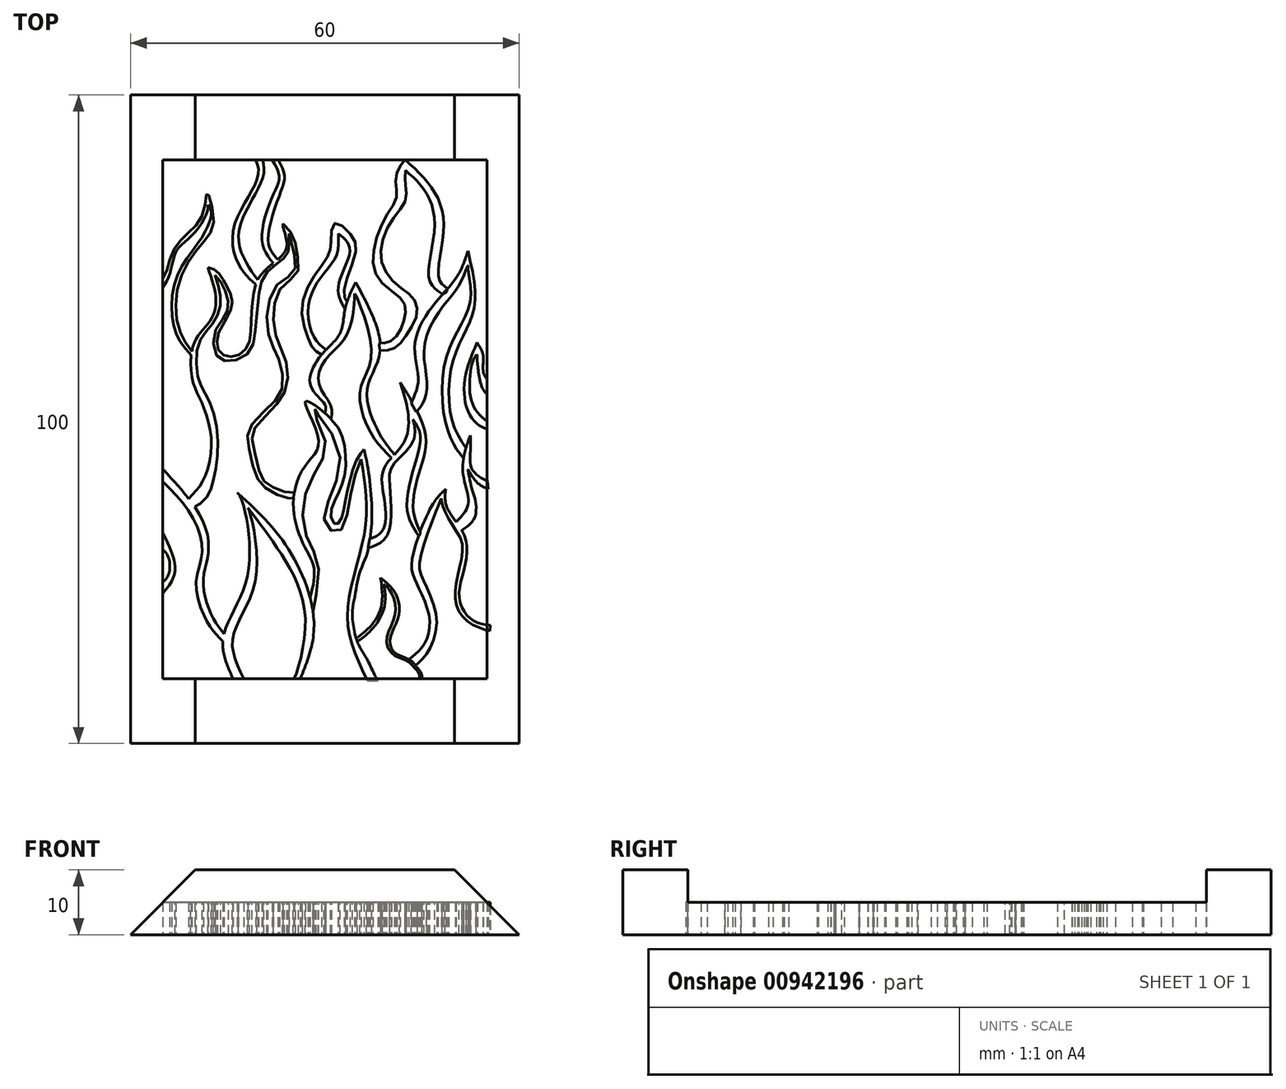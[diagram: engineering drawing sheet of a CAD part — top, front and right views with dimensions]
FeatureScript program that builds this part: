
annotation { "Feature Type Name" : "Feature", "Feature Type Description" : "" }
export const myFeature = defineFeature(function(context is Context, id is Id, definition is map)
    precondition{}
    {
        {
            var Q0;
            Q0=qCreatedBy(makeId("Top.planeOp"),FACE);
            var sketch = newSketch(context, id + "F0", { "sketchPlane" : qUnion([Q0])});
            skLineSegment(sketch, "E0.bottom", {"start": v(35, -50) * mm, "end": v(-35, -50) * mm});
            skLineSegment(sketch, "E0.top", {"start": v(35, 50) * mm, "end": v(-35, 50) * mm});
            skLineSegment(sketch, "E0.left", {"start": v(35, -50) * mm, "end": v(35, 50) * mm});
            skLineSegment(sketch, "E0.right", {"start": v(-35, -50) * mm, "end": v(-35, 50) * mm});
            skPoint(sketch, "E0.middle", {"position": v(0, 0) * mm});
            skLineSegment(sketch, "E1.bottom", {"start": v(25, -40) * mm, "end": v(-25, -40) * mm});
            skLineSegment(sketch, "E1.top", {"start": v(25, 40) * mm, "end": v(-25, 40) * mm});
            skLineSegment(sketch, "E1.left", {"start": v(25, -40) * mm, "end": v(25, 40) * mm});
            skLineSegment(sketch, "E1.right", {"start": v(-25, -40) * mm, "end": v(-25, 40) * mm});
            skSolve(sketch);
        }
        {
            var Q0;
            Q0=makeQuery(id+"F0.imprint","IMPRINT",FACE,{"disambiguationData":[TD([[makeQuery(id+"F0.imprint","IMPRINT",EDGE,{"derivedFrom":sQuery(id+"F0.wireOp",EDGE,"E0.bottom")}),-1.0]])]});
            extrude(context, id + "F1", {"entities" : qUnion([Q0]), "depth" : 10 * mm, "offsetDistance" : 25 * mm});
        }
        {
            var Q0;
            Q0=qCreatedBy(makeId("Top.planeOp"),FACE);
            var sketch = newSketch(context, id + "F2", { "sketchPlane" : qUnion([Q0])});
            skFitSpline(sketch, "E2", {"points": [v(-13.68, -40.96) * mm, v(-15.7, -33.78) * mm, v(-11.88, -23.84) * mm, v(-12.94, -12.18) * mm, v(-13.5, -11.32) * mm], "startDerivative": vector(-13.53, 27.29) * mm, "endDerivative": vector(-5.48, 5.3) * mm});
            skFitSpline(sketch, "E3", {"points": [v(-4.14, -40.79) * mm, v(-1.68, -31.66) * mm, v(-5.82, -19.7) * mm, v(-13.33, -11.5) * mm], "startDerivative": vector(12.17, 28.05) * mm, "endDerivative": vector(-23.9, 21.92) * mm});
            skFitSpline(sketch, "E4", {"points": [v(-12.05, -40.9) * mm, v(-14.21, -33.8) * mm, v(-10.6, -24.24) * mm, v(-11.88, -13.66) * mm, v(-11.96, -13.62) * mm], "startDerivative": vector(-13.14, 24.91) * mm, "endDerivative": vector(-2.3, -0.16) * mm});
            skFitSpline(sketch, "E5", {"points": [v(-11.88, -13.66) * mm, v(-7.03, -20.33) * mm, v(-3, -31.3) * mm, v(-5.12, -40.6) * mm, v(-5.34, -40.6) * mm], "startDerivative": vector(16.42, -21.5) * mm, "endDerivative": vector(-4.05, 2.08) * mm});
            skLineSegment(sketch, "E6", {"start": v(-13.68, -40.96) * mm, "end": v(-12.05, -40.9) * mm});
            skLineSegment(sketch, "E7", {"start": v(-5.27, -40.63) * mm, "end": v(-4.14, -40.79) * mm});
            skFitSpline(sketch, "E8", {"points": [v(6.54, -40.33) * mm, v(3.48, -30.22) * mm, v(6.2, -16.97) * mm, v(5.6, -6.18) * mm], "startDerivative": vector(-14.57, 30.29) * mm, "endDerivative": vector(-5.39, 32.36) * mm});
            skFitSpline(sketch, "E9", {"points": [v(5.6, -6.18) * mm, v(4.25, -10.26) * mm, v(3.06, -16.12) * mm, v(1.7, -17.4) * mm, v(0, -16.04) * mm, v(1.02, -11.45) * mm, v(1.96, -3.97) * mm, v(-1.44, 1.38) * mm, v(-1.36, 1.46) * mm, v(-1.7, 1.38) * mm, v(0, -3.12) * mm, v(-1.02, -7.37) * mm, v(-3.31, -12.98) * mm, v(-2.46, -18.92) * mm, v(-0.93, -23.09) * mm, v(-1.83, -29.73) * mm, v(-1.8, -29.89) * mm], "startDerivative": vector(-21.95, -53.1) * mm, "endDerivative": vector(3.5, -6.25) * mm});
            skFitSpline(sketch, "E10", {"points": [v(-2.28, -27.52) * mm, v(-1.68, -23.08) * mm, v(-3.31, -19.3) * mm, v(-4.88, -12.98) * mm, v(-3, -7.15) * mm, v(-0.95, -3.22) * mm, v(-3, 2.71) * mm, v(0.98, 0) * mm, v(2.98, -3.79) * mm, v(3.13, -8.08) * mm, v(2.05, -11.5) * mm, v(0.91, -14.72) * mm, v(1.7, -16.22) * mm, v(2.55, -15.3) * mm, v(3.27, -11.93) * mm, v(3.89, -9.48) * mm, v(4.85, -6.44) * mm, v(6.03, -4.65) * mm, v(6.07, -4.58) * mm], "startDerivative": vector(19.2, 73.13) * mm, "endDerivative": vector(2, 5.91) * mm});
            skFitSpline(sketch, "E11", {"points": [v(6.03, -4.65) * mm, v(6.64, -7.51) * mm, v(7.21, -12.98) * mm, v(7.14, -17.3) * mm, v(6.39, -21.08) * mm, v(5.21, -24.16) * mm, v(4.67, -27.12) * mm, v(4.25, -29.81) * mm, v(5, -34.3) * mm, v(6.54, -37.12) * mm, v(8.17, -40.33) * mm, v(8.22, -40.33) * mm], "startDerivative": vector(7.1, -29.12) * mm, "endDerivative": vector(3.64, 2.07) * mm});
            skLineSegment(sketch, "E12", {"start": v(6.54, -40.33) * mm, "end": v(8.22, -40.33) * mm});
            skFitSpline(sketch, "E13", {"points": [v(4.83, -33.83) * mm, v(7.26, -31.67) * mm, v(8.82, -28.18) * mm, v(8.58, -24.55) * mm, v(8.55, -24.46) * mm], "startDerivative": vector(8.42, 6.64) * mm, "endDerivative": vector(-0.47, 1) * mm});
            skFitSpline(sketch, "E14", {"points": [v(8.55, -24.46) * mm, v(10.5, -26.26) * mm, v(11.46, -28.66) * mm, v(11.07, -31.3) * mm, v(10.05, -33.98) * mm, v(10.83, -36.02) * mm, v(12.93, -37.01) * mm, v(13.99, -37.97) * mm, v(14.98, -39.53) * mm, v(14.98, -40.02) * mm, v(15.04, -39.97) * mm], "startDerivative": vector(17.16, -13.23) * mm, "endDerivative": vector(3.49, 3.77) * mm});
            skFitSpline(sketch, "E15", {"points": [v(5, -34.3) * mm, v(6.01, -33.57) * mm, v(7.65, -31.96) * mm, v(9.28, -28.26) * mm, v(9.05, -25.37) * mm, v(9, -25.35) * mm], "startDerivative": vector(5.7, 3.92) * mm, "endDerivative": vector(-1.21, 0) * mm});
            skFitSpline(sketch, "E16", {"points": [v(9, -25.35) * mm, v(10.03, -26.43) * mm, v(10.88, -28.62) * mm, v(10.47, -31.3) * mm, v(9.54, -33.87) * mm, v(10.5, -36.27) * mm, v(12.79, -37.29) * mm, v(13.68, -38.18) * mm, v(14.64, -39.52) * mm, v(14.6, -40.15) * mm, v(14.62, -40.15) * mm], "startDerivative": vector(10.85, -9.73) * mm, "endDerivative": vector(2.03, 0.73) * mm});
            skLineSegment(sketch, "E17", {"start": v(14.62, -40.15) * mm, "end": v(15.04, -39.97) * mm});
            skLineSegment(sketch, "E18", {"start": v(-5.12, -40.6) * mm, "end": v(-4.14, -40.79) * mm});
            skFitSpline(sketch, "E19", {"points": [v(-15.56, -33.1) * mm, v(-17.49, -30.22) * mm, v(-18.76, -25.04) * mm, v(-18, -20.58) * mm, v(-19.84, -13.88) * mm, v(-25.8, -6.7) * mm, v(-25.8, -6.55) * mm], "startDerivative": vector(-13.61, 16.83) * mm, "endDerivative": vector(1.72, 3.21) * mm});
            skFitSpline(sketch, "E20", {"points": [v(-15.74, -34.27) * mm, v(-17.05, -32.86) * mm, v(-18.5, -30.61) * mm, v(-19.85, -25.1) * mm, v(-18.92, -20.42) * mm, v(-20.78, -14.5) * mm, v(-25.8, -8.85) * mm], "startDerivative": vector(-12.4, 12.53) * mm, "endDerivative": vector(-25.9, 24.82) * mm});
            skFitSpline(sketch, "E21", {"points": [v(-25.8, -27.84) * mm, v(-23.5, -24.7) * mm, v(-23.4, -21.27) * mm, v(-25.8, -16.02) * mm, v(-25.8, -16.12) * mm], "startDerivative": vector(9, 10.56) * mm, "endDerivative": vector(0.54, -3.22) * mm});
            skFitSpline(sketch, "E22", {"points": [v(-25.8, -25.64) * mm, v(-24.26, -24.26) * mm, v(-24.14, -21.32) * mm, v(-25.8, -19.4) * mm], "startDerivative": vector(5.94, 3.52) * mm, "endDerivative": vector(-6, 4.84) * mm});
            skLineSegment(sketch, "E23", {"start": v(-25.8, -16.02) * mm, "end": v(-25.8, -19.4) * mm});
            skLineSegment(sketch, "E24", {"start": v(-25.8, -25.64) * mm, "end": v(-25.8, -27.84) * mm});
            skLineSegment(sketch, "E25", {"start": v(-25.8, -6.55) * mm, "end": v(-25.8, -8.85) * mm});
            skFitSpline(sketch, "E26", {"points": [v(12.93, -37.01) * mm, v(14.9, -35.28) * mm, v(16.17, -31.12) * mm, v(14.1, -25.17) * mm, v(13.41, -21.86) * mm, v(16.56, -13.28) * mm, v(18.64, -10.78) * mm], "startDerivative": vector(16.34, 11.46) * mm, "endDerivative": vector(14.03, 12.97) * mm});
            skFitSpline(sketch, "E27", {"points": [v(18.64, -10.78) * mm, v(18.7, -13.28) * mm, v(20.28, -15.86) * mm, v(21.85, -19.07) * mm, v(21.42, -23.36) * mm, v(20.7, -27.21) * mm, v(21.64, -29.86) * mm, v(23.35, -31.29) * mm, v(25.2, -31.79) * mm, v(25.5, -31.79) * mm], "startDerivative": vector(-2.35, -23.17) * mm, "endDerivative": vector(5.85, 0.53) * mm});
            skFitSpline(sketch, "E28", {"points": [v(13.99, -37.97) * mm, v(15.62, -36.32) * mm, v(17.24, -31.06) * mm, v(15.22, -24.9) * mm, v(14.66, -21.72) * mm, v(17.5, -13.33) * mm, v(17.97, -12.23) * mm], "startDerivative": vector(13.15, 10.63) * mm, "endDerivative": vector(3.75, 8.26) * mm});
            skFitSpline(sketch, "E29", {"points": [v(17.97, -12.23) * mm, v(18.15, -13.26) * mm, v(19.56, -16.17) * mm, v(21.16, -19.07) * mm, v(20.7, -23.16) * mm, v(20.1, -27.3) * mm, v(21.02, -30.16) * mm, v(23.24, -31.9) * mm, v(25.44, -32.66) * mm, v(25.5, -32.64) * mm], "startDerivative": vector(0.96, -12.29) * mm, "endDerivative": vector(1.87, 1.95) * mm});
            skLineSegment(sketch, "E30", {"start": v(25.44, -32.66) * mm, "end": v(25.5, -31.79) * mm});
            skFitSpline(sketch, "E31", {"points": [v(-21.02, -12.25) * mm, v(-18.72, -9.3) * mm, v(-17.55, -2.84) * mm, v(-19.17, 2.92) * mm, v(-20.38, 5.9) * mm, v(-20.2, 11.72) * mm, v(-17.77, 15.05) * mm, v(-16.8, 18.34) * mm, v(-18.04, 23.41) * mm], "startDerivative": vector(22.52, 22.51) * mm, "endDerivative": vector(-13.58, 40.22) * mm});
            skFitSpline(sketch, "E32", {"points": [v(-18.04, 23.41) * mm, v(-16.54, 22.7) * mm, v(-15.28, 20.77) * mm, v(-14.32, 18.43) * mm, v(-14.98, 15.84) * mm, v(-16.36, 13.32) * mm, v(-16.3, 10.5) * mm, v(-14.32, 9.66) * mm, v(-11.98, 11.1) * mm, v(-11.38, 14.64) * mm, v(-11.14, 18.25) * mm, v(-10.35, 21.5) * mm, v(-7.95, 24.07) * mm, v(-5.9, 26.63) * mm, v(-6.5, 29.82) * mm, v(-6.5, 30.12) * mm], "startDerivative": vector(30.14, -9.52) * mm, "endDerivative": vector(2.2, 9.15) * mm});
            skFitSpline(sketch, "E33", {"points": [v(-6.5, 30.12) * mm, v(-5.1, 28.62) * mm, v(-4.27, 25.5) * mm, v(-4.33, 22.43) * mm, v(-6.61, 20.45) * mm, v(-7.93, 16.66) * mm, v(-7.33, 12.16) * mm, v(-6.01, 8.97) * mm, v(-5.95, 4.89) * mm, v(-8, 1.7) * mm, v(-10.94, -1.6) * mm, v(-11.12, -3.8) * mm, v(-9.91, -8.54) * mm, v(-8.9, -9.98) * mm, v(-6.43, -11.18) * mm, v(-4.72, -11.3) * mm], "startDerivative": vector(28.86, -24.13) * mm, "endDerivative": vector(32.47, 1.3) * mm});
            skFitSpline(sketch, "E34", {"points": [v(-4.84, -12.2) * mm, v(-5.26, -12.17) * mm, v(-6.52, -11.94) * mm, v(-9.35, -10.43) * mm, v(-10.67, -8.54) * mm, v(-11.78, -3.99) * mm, v(-11.63, -1.36) * mm, v(-8.45, 2.06) * mm, v(-6.54, 4.95) * mm, v(-7.03, 9.03) * mm, v(-8.26, 11.7) * mm, v(-8.9, 16.66) * mm, v(-7.03, 21.04) * mm, v(-4.83, 22.7) * mm, v(-4.77, 25.66) * mm, v(-5.5, 28.36) * mm, v(-5.55, 28.62) * mm], "startDerivative": vector(-15.62, 0.83) * mm, "endDerivative": vector(-1.94, 9.71) * mm});
            skFitSpline(sketch, "E35", {"points": [v(-5.54, 28.55) * mm, v(-5.54, 26.6) * mm, v(-5.98, 25.15) * mm, v(-7.72, 23.77) * mm, v(-9.7, 21.45) * mm, v(-10.28, 18.25) * mm, v(-10.67, 14.64) * mm, v(-11.44, 10.7) * mm, v(-14.32, 8.99) * mm, v(-16.54, 9.66) * mm, v(-16.97, 13.43) * mm, v(-15.28, 16.17) * mm, v(-14.92, 18.25) * mm, v(-15.82, 20.77) * mm, v(-16.94, 22.17) * mm], "startDerivative": vector(1.12, -33.36) * mm, "endDerivative": vector(-19.84, 21.36) * mm});
            skFitSpline(sketch, "E36", {"points": [v(-16.94, 22.17) * mm, v(-16.07, 18.25) * mm, v(-17.27, 14.82) * mm, v(-19.43, 11.72) * mm, v(-19.46, 6.1) * mm, v(-18.07, 3.27) * mm, v(-16.54, -2.69) * mm, v(-17.17, -9.3) * mm, v(-18.33, -12.18) * mm, v(-20.09, -13.51) * mm, v(-20.18, -13.38) * mm], "startDerivative": vector(12.64, -36.82) * mm, "endDerivative": vector(-1.95, 8.45) * mm});
            skFitSpline(sketch, "E37", {"points": [v(14.7, -17.3) * mm, v(13.64, -13.94) * mm, v(14.45, -8.54) * mm, v(15.56, -2.69) * mm, v(11.62, 5.7) * mm], "startDerivative": vector(-7.27, 16.15) * mm, "endDerivative": vector(-17.46, 27.77) * mm});
            skFitSpline(sketch, "E38", {"points": [v(11.62, 5.7) * mm, v(12.63, 2.16) * mm, v(12.43, -3.12) * mm, v(9.36, -7.15) * mm, v(8.82, -9.98) * mm, v(9.36, -13.94) * mm, v(8.82, -17.3) * mm, v(7, -18.41) * mm], "startDerivative": vector(7.74, -22.94) * mm, "endDerivative": vector(-19.54, -6.96) * mm});
            skFitSpline(sketch, "E39", {"points": [v(6.74, -19.85) * mm, v(8.07, -19.34) * mm, v(9.57, -17.95) * mm, v(10.24, -14.17) * mm, v(10, -9.9) * mm, v(10.36, -7.32) * mm, v(13.6, -3.48) * mm, v(13.6, 0) * mm], "startDerivative": vector(13.8, 4.22) * mm, "endDerivative": vector(-5.5, 23.35) * mm});
            skFitSpline(sketch, "E40", {"points": [v(13.6, 0) * mm, v(14.74, -2.64) * mm, v(13.6, -7.98) * mm, v(12.7, -13.99) * mm, v(13.6, -16.57) * mm, v(14.45, -17.98) * mm], "startDerivative": vector(8.76, -13.32) * mm, "endDerivative": vector(6.18, -9.74) * mm});
            skFitSpline(sketch, "E41", {"points": [v(20.28, -15.86) * mm, v(22.14, -12.9) * mm, v(21.28, -8.11) * mm, v(22.43, -2.47) * mm], "startDerivative": vector(8.97, 9.37) * mm, "endDerivative": vector(5.32, 15.26) * mm});
            skFitSpline(sketch, "E42", {"points": [v(22.43, -2.47) * mm, v(22.5, -4.33) * mm, v(22.71, -7.69) * mm, v(24.64, -9.33) * mm, v(25.07, -9.47) * mm], "startDerivative": vector(0.68, -6.66) * mm, "endDerivative": vector(2.73, -0.64) * mm});
            skFitSpline(sketch, "E43", {"points": [v(25.21, -10.78) * mm, v(23.57, -9.83) * mm, v(22.07, -7.69) * mm], "startDerivative": vector(-3.75, 1.64) * mm, "endDerivative": vector(-2.57, 4.48) * mm});
            skFitSpline(sketch, "E44", {"points": [v(22.07, -7.9) * mm, v(22.71, -10.78) * mm, v(23.28, -12.97) * mm, v(22.71, -15.86) * mm, v(21.12, -17.14) * mm, v(21.14, -17.18) * mm], "startDerivative": vector(2.3, -11.6) * mm, "endDerivative": vector(1.26, -0.85) * mm});
            skLineSegment(sketch, "E45", {"start": v(25.07, -9.47) * mm, "end": v(25.21, -10.78) * mm});
            skFitSpline(sketch, "E46", {"points": [v(21.77, -4.46) * mm, v(19.56, 0) * mm, v(19.56, 8.19) * mm, v(21.77, 13.75) * mm, v(23.2, 18.3) * mm, v(22.07, 25.97) * mm], "startDerivative": vector(-14.52, 22.01) * mm, "endDerivative": vector(-8.63, 36.95) * mm});
            skFitSpline(sketch, "E47", {"points": [v(22.07, 25.97) * mm, v(20.47, 22.13) * mm, v(16.93, 17.79) * mm, v(13.9, 11.73) * mm, v(14.4, 6.17) * mm, v(13.45, 2.79) * mm], "startDerivative": vector(-6.91, -21.62) * mm, "endDerivative": vector(-8.55, -18.89) * mm});
            skFitSpline(sketch, "E48", {"points": [v(21.38, -6.08) * mm, v(20.01, -4.08) * mm, v(18.51, 0) * mm, v(18.44, 8.35) * mm, v(20.87, 14.28) * mm, v(22.48, 18.35) * mm, v(22.07, 23.07) * mm], "startDerivative": vector(-12, 15.82) * mm, "endDerivative": vector(-5.67, 29.87) * mm});
            skFitSpline(sketch, "E49", {"points": [v(21.8, 23.07) * mm, v(20.37, 20.14) * mm, v(18, 17.14) * mm, v(15.37, 11.43) * mm, v(15.72, 5.92) * mm, v(15.3, 2.79) * mm, v(14.24, 1.25) * mm], "startDerivative": vector(-8.21, -19.86) * mm, "endDerivative": vector(-10.4, -11.91) * mm});
            skFitSpline(sketch, "E50", {"points": [v(21.8, 23.07) * mm, v(22.07, 23.68) * mm, v(22.07, 23.07) * mm], "startDerivative": vector(0.67, 1.83) * mm, "endDerivative": vector(-0.13, -1.86) * mm});
            skFitSpline(sketch, "E51", {"points": [v(-20.54, 10.46) * mm, v(-22.6, 14.22) * mm, v(-22.4, 21.4) * mm, v(-19.07, 26.95) * mm, v(-17.17, 30.5) * mm, v(-18.16, 34.83) * mm, v(-18.66, 32.1) * mm, v(-20.88, 28.87) * mm, v(-23.41, 25.97) * mm, v(-24.72, 22.1) * mm, v(-25.8, 21.1) * mm], "startDerivative": vector(-23.76, 32.34) * mm, "endDerivative": vector(-19.74, -11.85) * mm});
            skFitSpline(sketch, "E52", {"points": [v(-25.43, 19.76) * mm, v(-24.03, 22.1) * mm, v(-22.88, 25.97) * mm, v(-20.3, 28.56) * mm, v(-18.1, 32.1) * mm, v(-18.03, 33.05) * mm], "startDerivative": vector(8.31, 10.66) * mm, "endDerivative": vector(-0.68, 6.9) * mm});
            skFitSpline(sketch, "E53", {"points": [v(-18.03, 33.05) * mm, v(-17.5, 32.1) * mm, v(-17.81, 30.47) * mm, v(-19.46, 27.33) * mm, v(-23, 21.55) * mm, v(-23.14, 13.72) * mm, v(-21.6, 10.97) * mm, v(-20.62, 9.86) * mm], "startDerivative": vector(8.22, -10.57) * mm, "endDerivative": vector(9.73, -10.53) * mm});
            skLineSegment(sketch, "E54", {"start": v(-25.8, 21.1) * mm, "end": v(-25.43, 19.76) * mm});
            skFitSpline(sketch, "E55", {"points": [v(10.28, -5.97) * mm, v(7.21, -2.31) * mm, v(5.45, 4.47) * mm, v(7.21, 10.4) * mm, v(4.67, 19.26) * mm, v(4.6, 19.33) * mm], "startDerivative": vector(-15.6, 15.08) * mm, "endDerivative": vector(-1.73, 0.72) * mm});
            skFitSpline(sketch, "E56", {"points": [v(4.6, 19.33) * mm, v(4.38, 16.69) * mm, v(3.13, 12.55) * mm, v(0, 9.05) * mm, v(-0.9, 5.4) * mm, v(0.88, 2.19) * mm, v(0.98, 0) * mm], "startDerivative": vector(-0.91, -16.9) * mm, "endDerivative": vector(-2.28, -16.26) * mm});
            skFitSpline(sketch, "E57", {"points": [v(10.74, -5.46) * mm, v(9.7, -4.16) * mm, v(8.28, -1.94) * mm, v(6.51, 4.42) * mm, v(8.53, 10.59) * mm, v(4.75, 21.14) * mm], "startDerivative": vector(-9.25, 11.1) * mm, "endDerivative": vector(-20.8, 38.74) * mm});
            skFitSpline(sketch, "E58", {"points": [v(4.75, 21.14) * mm, v(3.13, 17) * mm, v(2.32, 13.21) * mm, v(-0.5, 9.93) * mm, v(-2.22, 5.23) * mm, v(0, 2.25) * mm, v(0, 0.94) * mm], "startDerivative": vector(-10.72, -22.22) * mm, "endDerivative": vector(-3.65, -12.61) * mm});
            skFitSpline(sketch, "E59", {"points": [v(18.19, 19.26) * mm, v(16.1, 21.64) * mm, v(16.93, 29.69) * mm, v(15.37, 35.31) * mm, v(12.43, 38.37) * mm], "startDerivative": vector(-13.95, 9.15) * mm, "endDerivative": vector(-13.94, 12.17) * mm});
            skFitSpline(sketch, "E60", {"points": [v(12.43, 38.37) * mm, v(12.43, 36.16) * mm, v(12.43, 33.78) * mm, v(10.23, 30.47) * mm, v(8.61, 25.37) * mm, v(10.48, 21.3) * mm, v(13.48, 18.83) * mm, v(14.22, 16.37) * mm, v(12.43, 12.71) * mm, v(10.57, 10.84) * mm, v(8.53, 10.59) * mm], "startDerivative": vector(-1.23, -26.61) * mm, "endDerivative": vector(-27.02, 0.36) * mm});
            skFitSpline(sketch, "E61", {"points": [v(18.95, 20.14) * mm, v(17.56, 21.82) * mm, v(18.34, 29.63) * mm, v(16.48, 35.7) * mm, v(12.43, 39.96) * mm], "startDerivative": vector(-11.2, 7.48) * mm, "endDerivative": vector(-16.77, 15.22) * mm});
            skFitSpline(sketch, "E62", {"points": [v(12.34, 40.02) * mm, v(11.26, 38.37) * mm, v(10.96, 36.11) * mm, v(11.02, 34.01) * mm, v(9.27, 31) * mm, v(7.47, 25.36) * mm, v(8.53, 21.3) * mm, v(11.92, 18.45) * mm, v(12.43, 16.6) * mm, v(11.86, 14.13) * mm, v(10.48, 12.27) * mm, v(9.1, 11.73) * mm, v(8.53, 11.79) * mm], "startDerivative": vector(-17.07, -21) * mm, "endDerivative": vector(-12.69, 3.07) * mm});
            skFitSpline(sketch, "E63", {"points": [v(0.2, 10.7) * mm, v(-1.6, 12.5) * mm, v(-2.55, 17.34) * mm, v(-0.68, 21.8) * mm, v(1.74, 25.15) * mm, v(2.1, 28.62) * mm], "startDerivative": vector(-11.98, 8.84) * mm, "endDerivative": vector(-0.7, 19.12) * mm});
            skFitSpline(sketch, "E64", {"points": [v(2.1, 28.62) * mm, v(3.86, 26.14) * mm, v(2.1, 20.53) * mm, v(3.13, 17) * mm], "startDerivative": vector(9.08, -7.22) * mm, "endDerivative": vector(5.87, -10.14) * mm});
            skFitSpline(sketch, "E65", {"points": [v(3.5, 18.06) * mm, v(3.13, 18.51) * mm, v(3.13, 20.69) * mm, v(4.82, 26.14) * mm, v(3.86, 28.62) * mm, v(1.54, 30.23) * mm, v(0.93, 27.45) * mm, v(0.68, 25.54) * mm, v(-1.34, 22.5) * mm, v(-3.51, 17.45) * mm, v(-2.6, 12.5) * mm, v(-1.6, 10.63) * mm, v(-0.5, 9.93) * mm], "startDerivative": vector(-11.02, 9.42) * mm, "endDerivative": vector(20.47, -10.24) * mm});
            skFitSpline(sketch, "E66", {"points": [v(25.5, -0.71) * mm, v(22.6, 2.86) * mm, v(22.86, 9.03) * mm, v(23.46, 9.93) * mm], "startDerivative": vector(-9.5, 7.42) * mm, "endDerivative": vector(3.32, 3.21) * mm});
            skFitSpline(sketch, "E67", {"points": [v(23.46, 10) * mm, v(23.63, 7.78) * mm, v(24.65, 4.22) * mm, v(26.77, 3.11) * mm], "startDerivative": vector(0.35, -6.56) * mm, "endDerivative": vector(7.68, -2.05) * mm});
            skFitSpline(sketch, "E68", {"points": [v(25.16, -1.6) * mm, v(23.46, -0.71) * mm, v(21.77, 2.18) * mm, v(21.77, 7.02) * mm, v(23.46, 11.7) * mm], "startDerivative": vector(-9.6, 3.52) * mm, "endDerivative": vector(6.85, 15.64) * mm});
            skFitSpline(sketch, "E69", {"points": [v(23.54, 11.7) * mm, v(24.4, 9.93) * mm, v(24.48, 7.19) * mm, v(25.5, 5.57) * mm], "startDerivative": vector(3.5, -5) * mm, "endDerivative": vector(4.19, -4.54) * mm});
            skLineSegment(sketch, "E70", {"start": v(25.5, 5.57) * mm, "end": v(26.77, 3.11) * mm});
            skLineSegment(sketch, "E71", {"start": v(25.5, -0.71) * mm, "end": v(25.16, -1.6) * mm});
            skFitSpline(sketch, "E72", {"points": [v(-10.35, 21.5) * mm, v(-12.41, 24.65) * mm, v(-13.27, 28.94) * mm, v(-11, 34.24) * mm, v(-9.38, 38.24) * mm, v(-9.89, 40.86) * mm], "startDerivative": vector(-11.57, 15.53) * mm, "endDerivative": vector(-5.45, 15.71) * mm});
            skFitSpline(sketch, "E73", {"points": [v(-7.95, 24.07) * mm, v(-9.7, 27.6) * mm, v(-7.95, 34.68) * mm, v(-7.03, 37.56) * mm, v(-9.7, 42.19) * mm], "startDerivative": vector(-10.64, 13.1) * mm, "endDerivative": vector(-14.14, 19.06) * mm});
            skFitSpline(sketch, "E74", {"points": [v(-7.24, 24.65) * mm, v(-7.97, 25.44) * mm, v(-8.76, 27.74) * mm, v(-7, 34.57) * mm, v(-6.23, 37.55) * mm, v(-7.54, 40.65) * mm], "startDerivative": vector(-6.15, 5.96) * mm, "endDerivative": vector(-8.79, 15.54) * mm});
            skFitSpline(sketch, "E75", {"points": [v(-11.03, 40.7) * mm, v(-10.22, 38.31) * mm, v(-11.58, 34.7) * mm, v(-14.13, 29.22) * mm, v(-13.53, 24.34) * mm, v(-12.05, 22.13) * mm, v(-10.66, 20.78) * mm], "startDerivative": vector(8.54, -16.2) * mm, "endDerivative": vector(11.32, -10.4) * mm});
            skLineSegment(sketch, "E76", {"start": v(-11.03, 40.7) * mm, "end": v(-9.89, 40.86) * mm});
            skLineSegment(sketch, "E77", {"start": v(-7.54, 40.65) * mm, "end": v(-9.7, 42.19) * mm});
            skLineSegment(sketch, "E78", {"start": v(-13.5, -11.32) * mm, "end": v(-13.33, -11.5) * mm});
            skLineSegment(sketch, "E79", {"start": v(-21.02, -12.25) * mm, "end": v(-21.02, -12.4) * mm});
            skLineSegment(sketch, "E80", {"start": v(-21.02, -12.4) * mm, "end": v(-20.2, -13.42) * mm});
            skLineSegment(sketch, "E81", {"start": v(-20.2, -13.42) * mm, "end": v(-20.18, -13.38) * mm});
            skLineSegment(sketch, "E82", {"start": v(-4.84, -12.2) * mm, "end": v(-4.72, -12.14) * mm});
            skLineSegment(sketch, "E83", {"start": v(-4.72, -12.14) * mm, "end": v(-4.64, -11.4) * mm});
            skLineSegment(sketch, "E84", {"start": v(-4.64, -11.4) * mm, "end": v(-4.73, -11.31) * mm});
            skLineSegment(sketch, "E85", {"start": v(23.46, 9.93) * mm, "end": v(23.46, 10) * mm});
            skLineSegment(sketch, "E86", {"start": v(18.19, 19.26) * mm, "end": v(18.95, 20.14) * mm});
            skLineSegment(sketch, "E87", {"start": v(8.53, 11.79) * mm, "end": v(8.4, 11.44) * mm});
            skLineSegment(sketch, "E88", {"start": v(8.4, 11.44) * mm, "end": v(8.53, 10.59) * mm});
            skLineSegment(sketch, "E89", {"start": v(12.43, 39.96) * mm, "end": v(12.43, 40.12) * mm});
            skLineSegment(sketch, "E90", {"start": v(12.43, 40.12) * mm, "end": v(12.34, 40.02) * mm});
            skLineSegment(sketch, "E91", {"start": v(12.93, -37.01) * mm, "end": v(13.3, -37.4) * mm});
            skLineSegment(sketch, "E92", {"start": v(13.3, -37.4) * mm, "end": v(13.98, -37.98) * mm});
            skLineSegment(sketch, "E93", {"start": v(4.83, -33.83) * mm, "end": v(4.86, -34.22) * mm});
            skLineSegment(sketch, "E94", {"start": v(4.86, -34.22) * mm, "end": v(5, -34.3) * mm});
            skLineSegment(sketch, "E95", {"start": v(6.74, -19.85) * mm, "end": v(6.68, -19.85) * mm});
            skLineSegment(sketch, "E96", {"start": v(6.68, -19.85) * mm, "end": v(6.91, -18.4) * mm});
            skLineSegment(sketch, "E97", {"start": v(6.91, -18.4) * mm, "end": v(7, -18.41) * mm});
            skLineSegment(sketch, "E98", {"start": v(21.14, -17.18) * mm, "end": v(20.4, -16.57) * mm});
            skLineSegment(sketch, "E99", {"start": v(20.4, -16.57) * mm, "end": v(20.28, -15.85) * mm});
            skLineSegment(sketch, "E100", {"start": v(22.07, -7.9) * mm, "end": v(22.07, -7.69) * mm});
            skLineSegment(sketch, "E101", {"start": v(23.46, 11.7) * mm, "end": v(23.52, 11.84) * mm});
            skLineSegment(sketch, "E102", {"start": v(23.52, 11.84) * mm, "end": v(23.54, 11.7) * mm});
            skLineSegment(sketch, "E103", {"start": v(18.19, 19.26) * mm, "end": v(18.81, 19.67) * mm});
            skLineSegment(sketch, "E104", {"start": v(18.81, 19.67) * mm, "end": v(18.95, 20.14) * mm});
            skLineSegment(sketch, "E105", {"start": v(13.45, 2.79) * mm, "end": v(13.32, 2.46) * mm});
            skLineSegment(sketch, "E106", {"start": v(13.32, 2.46) * mm, "end": v(14.1, 1.12) * mm});
            skLineSegment(sketch, "E107", {"start": v(14.1, 1.12) * mm, "end": v(14.24, 1.26) * mm});
            skLineSegment(sketch, "E108", {"start": v(10.28, -5.97) * mm, "end": v(10.71, -5.84) * mm});
            skLineSegment(sketch, "E109", {"start": v(10.71, -5.84) * mm, "end": v(10.75, -5.46) * mm});
            skLineSegment(sketch, "E110", {"start": v(10.74, -5.46) * mm, "end": v(10.75, -5.46) * mm});
            skLineSegment(sketch, "E111", {"start": v(13.98, -37.98) * mm, "end": v(13.99, -37.97) * mm});
            skLineSegment(sketch, "E112", {"start": v(5, -34.3) * mm, "end": v(5, -34.3) * mm});
            skLineSegment(sketch, "E113", {"start": v(14.45, -17.98) * mm, "end": v(14.65, -17.9) * mm});
            skLineSegment(sketch, "E114", {"start": v(14.65, -17.9) * mm, "end": v(14.75, -17.34) * mm});
            skLineSegment(sketch, "E115", {"start": v(14.75, -17.34) * mm, "end": v(14.7, -17.3) * mm});
            skLineSegment(sketch, "E116", {"start": v(21.14, -17.18) * mm, "end": v(21.13, -17.17) * mm});
            skLineSegment(sketch, "E117", {"start": v(21.13, -17.17) * mm, "end": v(21.12, -17.14) * mm});
            skLineSegment(sketch, "E118", {"start": v(21.12, -17.14) * mm, "end": v(21.14, -17.18) * mm});
            skLineSegment(sketch, "E119", {"start": v(20.28, -15.85) * mm, "end": v(20.28, -15.86) * mm});
            skLineSegment(sketch, "E120", {"start": v(20.28, -15.86) * mm, "end": v(20.28, -15.86) * mm});
            skLineSegment(sketch, "E121", {"start": v(-5.55, 28.62) * mm, "end": v(-5.54, 28.55) * mm});
            skLineSegment(sketch, "E122", {"start": v(7, -18.41) * mm, "end": v(7, -18.41) * mm});
            skLineSegment(sketch, "E123", {"start": v(14.62, -40.15) * mm, "end": v(14.98, -40.02) * mm});
            skLineSegment(sketch, "E124", {"start": v(14.98, -40.02) * mm, "end": v(14.98, -40) * mm});
            skLineSegment(sketch, "E125", {"start": v(14.98, -40) * mm, "end": v(14.97, -39.98) * mm});
            skSolve(sketch);
        }
        {
            var Q0;
            {var subQ3=sQuery(id+"F2.wireOp",EDGE,"E22");Q0=makeQuery(id+"F2.imprint","IMPRINT",FACE,{"disambiguationData":[TD([[makeQuery(id+"F2.imprint","IMPRINT",EDGE,{"derivedFrom":subQ3}),-1.0]])]});}
            extrude(context, id + "F3", {"entities" : qUnion([Q0]), "operationType" : NewBodyOperationType.ADD, "depth" : 5 * mm, "offsetDistance" : 25 * mm});
        }
        {
            var Q0;
            {var subQ6=sQuery(id+"F2.wireOp",EDGE,"E20");Q0=makeQuery(id+"F2.imprint","IMPRINT",FACE,{"disambiguationData":[TD([[makeQuery(id+"F2.imprint","IMPRINT",EDGE,{"derivedFrom":subQ6}),-1.0]])]});}
            var Q1;
            {var subQ0=sQuery(id+"F2.wireOp",EDGE,"E6");Q1=makeQuery(id+"F2.imprint","IMPRINT",FACE,{"disambiguationData":[TD([[makeQuery(id+"F2.imprint","IMPRINT",EDGE,{"derivedFrom":subQ0}),1.0]])]});}
            var Q2;
            {var subQ15=sQuery(id+"F2.wireOp",EDGE,"E33");Q2=makeQuery(id+"F2.imprint","IMPRINT",FACE,{"disambiguationData":[TD([[makeQuery(id+"F2.imprint","IMPRINT",EDGE,{"derivedFrom":subQ15}),-1.0]])]});}
            var Q3;
            {var subQ0=sQuery(id+"F2.wireOp",EDGE,"E79");Q3=makeQuery(id+"F2.imprint","IMPRINT",FACE,{"disambiguationData":[TD([[makeQuery(id+"F2.imprint","IMPRINT",EDGE,{"derivedFrom":subQ0}),1.0]])]});}
            var Q4;
            {var subQ0=sQuery(id+"F2.wireOp",EDGE,"E36");var subQ1=sQuery(id+"F2.wireOp",EDGE,"E19");var subQ2=makeQuery(id+"F2.imprint","INTERSECT",VERTEX,{"disambiguationData":[OD(0.0)],"derivedFrom":[subQ1,subQ0]});Q4=makeQuery(id+"F2.imprint","IMPRINT",FACE,{"disambiguationData":[TD([[makeQuery(id+"F2.imprint","IMPRINT",EDGE,{"disambiguationData":[TD([[subQ2,1.0]])],"derivedFrom":subQ1}),1.0]])]});}
            extrude(context, id + "F4", {"entities" : qUnion([Q0, Q1, Q2, Q3, Q4]), "operationType" : NewBodyOperationType.ADD, "depth" : 5 * mm, "offsetDistance" : 25 * mm});
        }
        {
            var Q0;
            {var subQ1=sQuery(id+"F2.wireOp",EDGE,"E51");Q0=makeQuery(id+"F2.imprint","IMPRINT",FACE,{"disambiguationData":[TD([[makeQuery(id+"F2.imprint","IMPRINT",EDGE,{"derivedFrom":subQ1}),1.0]])]});}
            var Q1;
            {var subQ0=sQuery(id+"F2.wireOp",EDGE,"E72");Q1=makeQuery(id+"F2.imprint","IMPRINT",FACE,{"disambiguationData":[TD([[makeQuery(id+"F2.imprint","IMPRINT",EDGE,{"derivedFrom":subQ0}),1.0]])]});}
            extrude(context, id + "F5", {"entities" : qUnion([Q0, Q1]), "operationType" : NewBodyOperationType.ADD, "depth" : 5 * mm, "offsetDistance" : 25 * mm});
        }
        {
            var Q0;
            {var subQ0=sQuery(id+"F2.wireOp",EDGE,"E73");Q0=makeQuery(id+"F2.imprint","IMPRINT",FACE,{"disambiguationData":[TD([[makeQuery(id+"F2.imprint","IMPRINT",EDGE,{"derivedFrom":subQ0}),-1.0]])]});}
            var Q1;
            {var subQ1=sQuery(id+"F2.wireOp",EDGE,"E63");Q1=makeQuery(id+"F2.imprint","IMPRINT",FACE,{"disambiguationData":[TD([[makeQuery(id+"F2.imprint","IMPRINT",EDGE,{"derivedFrom":subQ1}),1.0]])]});}
            var Q2;
            Q2=makeQuery(id+"F2.imprint","IMPRINT",FACE,{"disambiguationData":[TD([[makeQuery(id+"F2.imprint","IMPRINT",EDGE,{"derivedFrom":sQuery(id+"F2.wireOp",EDGE,"E59")}),-1.0]])]});
            var Q3;
            {var subQ2=sQuery(id+"F2.wireOp",EDGE,"E87");Q3=makeQuery(id+"F2.imprint","IMPRINT",FACE,{"disambiguationData":[TD([[makeQuery(id+"F2.imprint","IMPRINT",EDGE,{"derivedFrom":subQ2}),1.0]])]});}
            var Q4;
            Q4=makeQuery(id+"F2.imprint","IMPRINT",FACE,{"disambiguationData":[TD([[makeQuery(id+"F2.imprint","IMPRINT",EDGE,{"derivedFrom":sQuery(id+"F2.wireOp",EDGE,"E66")}),1.0]])]});
            var Q5;
            {var subQ9=sQuery(id+"F2.wireOp",EDGE,"E46");Q5=makeQuery(id+"F2.imprint","IMPRINT",FACE,{"disambiguationData":[TD([[makeQuery(id+"F2.imprint","IMPRINT",EDGE,{"derivedFrom":subQ9}),1.0]])]});}
            var Q6;
            {var subQ5=sQuery(id+"F2.wireOp",EDGE,"E106");Q6=makeQuery(id+"F2.imprint","IMPRINT",FACE,{"disambiguationData":[TD([[makeQuery(id+"F2.imprint","IMPRINT",EDGE,{"derivedFrom":subQ5}),1.0]])]});}
            extrude(context, id + "F6", {"entities" : qUnion([Q0, Q1, Q2, Q3, Q4, Q5, Q6]), "operationType" : NewBodyOperationType.ADD, "depth" : 5 * mm, "offsetDistance" : 25 * mm});
        }
        {
            var Q0;
            {var subQ0=sQuery(id+"F2.wireOp",EDGE,"E42");Q0=makeQuery(id+"F2.imprint","IMPRINT",FACE,{"disambiguationData":[TD([[makeQuery(id+"F2.imprint","IMPRINT",EDGE,{"derivedFrom":subQ0}),-1.0]])]});}
            var Q1;
            {var subQ3=sQuery(id+"F2.wireOp",EDGE,"E99");var subQ5=sQuery(id+"F2.wireOp",EDGE,"E98");var subQ7=makeQuery(id+"F2.imprint","INTERSECT",VERTEX,{"derivedFrom":[subQ5,subQ3]});Q1=makeQuery(id+"F2.imprint","IMPRINT",FACE,{"disambiguationData":[TD([[makeQuery(id+"F2.imprint","IMPRINT",EDGE,{"disambiguationData":[TD([[subQ7,1.0]])],"derivedFrom":subQ5}),-1.0]])]});}
            var Q2;
            {var subQ1=sQuery(id+"F2.wireOp",EDGE,"E28");Q2=makeQuery(id+"F2.imprint","IMPRINT",FACE,{"disambiguationData":[TD([[makeQuery(id+"F2.imprint","IMPRINT",EDGE,{"derivedFrom":subQ1}),1.0]])]});}
            extrude(context, id + "F7", {"entities" : qUnion([Q0, Q1, Q2]), "depth" : 5 * mm, "offsetDistance" : 25 * mm});
        }
        {
            var Q0;
            {var subQ15=sQuery(id+"F2.wireOp",EDGE,"E55");Q0=makeQuery(id+"F2.imprint","IMPRINT",FACE,{"disambiguationData":[TD([[makeQuery(id+"F2.imprint","IMPRINT",EDGE,{"derivedFrom":subQ15}),-1.0]])]});}
            var Q1;
            {var subQ12=sQuery(id+"F2.wireOp",EDGE,"E39");Q1=makeQuery(id+"F2.imprint","IMPRINT",FACE,{"disambiguationData":[TD([[makeQuery(id+"F2.imprint","IMPRINT",EDGE,{"derivedFrom":subQ12}),1.0]])]});}
            var Q2;
            {var subQ4=sQuery(id+"F2.wireOp",EDGE,"E108");Q2=makeQuery(id+"F2.imprint","IMPRINT",FACE,{"disambiguationData":[TD([[makeQuery(id+"F2.imprint","IMPRINT",EDGE,{"derivedFrom":subQ4}),1.0]])]});}
            var Q3;
            {var subQ2=sQuery(id+"F2.wireOp",EDGE,"E113");Q3=makeQuery(id+"F2.imprint","IMPRINT",FACE,{"disambiguationData":[TD([[makeQuery(id+"F2.imprint","IMPRINT",EDGE,{"derivedFrom":subQ2}),1.0]])]});}
            var Q4;
            {var subQ1=sQuery(id+"F2.wireOp",EDGE,"E95");Q4=makeQuery(id+"F2.imprint","IMPRINT",FACE,{"disambiguationData":[TD([[makeQuery(id+"F2.imprint","IMPRINT",EDGE,{"derivedFrom":subQ1}),-1.0]])]});}
            extrude(context, id + "F8", {"entities" : qUnion([Q0, Q1, Q2, Q3, Q4]), "depth" : 5 * mm, "offsetDistance" : 25 * mm});
        }
        {
            var Q0;
            {var subQ18=sQuery(id+"F2.wireOp",EDGE,"E8");Q0=makeQuery(id+"F2.imprint","IMPRINT",FACE,{"disambiguationData":[TD([[makeQuery(id+"F2.imprint","IMPRINT",EDGE,{"derivedFrom":subQ18}),-1.0]])]});}
            var Q1;
            {var subQ0=sQuery(id+"F2.wireOp",EDGE,"E82");Q1=makeQuery(id+"F2.imprint","IMPRINT",FACE,{"disambiguationData":[TD([[makeQuery(id+"F2.imprint","IMPRINT",EDGE,{"derivedFrom":subQ0}),1.0]])]});}
            var Q2;
            {var subQ0=sQuery(id+"F2.wireOp",EDGE,"E93");Q2=makeQuery(id+"F2.imprint","IMPRINT",FACE,{"disambiguationData":[TD([[makeQuery(id+"F2.imprint","IMPRINT",EDGE,{"derivedFrom":subQ0}),1.0]])]});}
            extrude(context, id + "F9", {"entities" : qUnion([Q0, Q1, Q2]), "depth" : 5 * mm, "offsetDistance" : 25 * mm});
        }
        {
            var Q0;
            {var subQ0=sQuery(id+"F2.wireOp",EDGE,"E16");var subQ1=sQuery(id+"F2.wireOp",EDGE,"E15");var subQ2=makeQuery(id+"F2.imprint","INTERSECT",VERTEX,{"disambiguationData":[OD(0.0)],"derivedFrom":[subQ1,subQ0]});Q0=makeQuery(id+"F2.imprint","IMPRINT",FACE,{"disambiguationData":[TD([[makeQuery(id+"F2.imprint","IMPRINT",EDGE,{"disambiguationData":[TD([[subQ2,1.0]])],"derivedFrom":subQ1}),1.0]])]});}
            var Q1;
            {var subQ13=sQuery(id+"F2.wireOp",EDGE,"E13");Q1=makeQuery(id+"F2.imprint","IMPRINT",FACE,{"disambiguationData":[TD([[makeQuery(id+"F2.imprint","IMPRINT",EDGE,{"derivedFrom":subQ13}),-1.0]])]});}
            var Q2;
            {var subQ0=sQuery(id+"F2.wireOp",EDGE,"E91");Q2=makeQuery(id+"F2.imprint","IMPRINT",FACE,{"disambiguationData":[TD([[makeQuery(id+"F2.imprint","IMPRINT",EDGE,{"derivedFrom":subQ0}),1.0]])]});}
            extrude(context, id + "F10", {"entities" : qUnion([Q0, Q1, Q2]), "depth" : 5 * mm, "offsetDistance" : 25 * mm});
        }
        {
            var Q0;
            Q0=makeQuery(id+"F1.opExtrude","CAP_EDGE",EDGE,{"disambiguationData":[OSD([sQuery(id+"F0.wireOp",EDGE,"E0.right")])],"isStart":false});
            var Q1;
            Q1=makeQuery(id+"F1.opExtrude","CAP_EDGE",EDGE,{"disambiguationData":[OSD([sQuery(id+"F0.wireOp",EDGE,"E0.left")])],"isStart":false});
            chamfer(context, id + "F11", {"entities" : qUnion([Q0, Q1]), "width" : 15 * mm, "tangentPropagation" : true});
        }
    });
